# Revit family: Farola Solar Moon S blanca
name_source: partatom
category: Luminarias
units: mm (PartAtom-declared; Revit-internal decimal feet)

## family parameters
Compartido = Sí
Corte con vacíos al cargar = No
Cota de conector redondo = Diámetro de uso
Origen de luz = No
Punto de cálculo de habitación = No
Se basa en plano de trabajo = No
Siempre vertical = Sí
Tipo de pieza = Normal

## types (2) — shared parameters
Altura columna extremos = 4000 mm  [stored 13.1234 ft]
Altura columna planos = 4000 mm  [stored 13.1234 ft]
Clase eficiencia energética = A++
Distancia brazo-final de columna = 3500 mm  [stored 11.4829 ft]
Distancia inserto-columa = 3864 mm
Elevación por defecto = 2000 mm  [stored 6.56168 ft]
Fabricante = Ekiona
Marcado CE = SÍ
URL = https://www.ekiona.com
URL producto = https://ekiona.com

## per-type parameters (varying)
| type | Descripción | Descripción de la empresa | Dirección | Gama de acabados | Gama de colores | Garantía | Modelo |
| Farola Olintu S pintura blanca | Farola solar que combina diseño y eficencia |  |  |  |  | 2 años | Modelo Olintu |
| Farola Olintu S pintura gris | Farola solar compacta y estética, la unión entre eficiencia y diseño | Diseñamos, desarrollamos, fabricamos y comercializamos farolas solares que se adaptan a cualquier necesidad. | Parque Tecnológico Miramón - Paseo Mikeletegi 56 - 20009 Donostia/San Sebastián | Galvanizado, Fibra de vidrio, Aluminio | Blanco, Negro, Gris, Verde bosque, acero galvanizado | 5 años | Modelo Moon |

note: [stored X ft] marks values corroborated as IEEE doubles in the binary element streams (Revit-internal decimal feet)

## geometry (parser evidence)
native form markers: Blend x8, Sweep x13
no freeform markers — native parametric forms only
